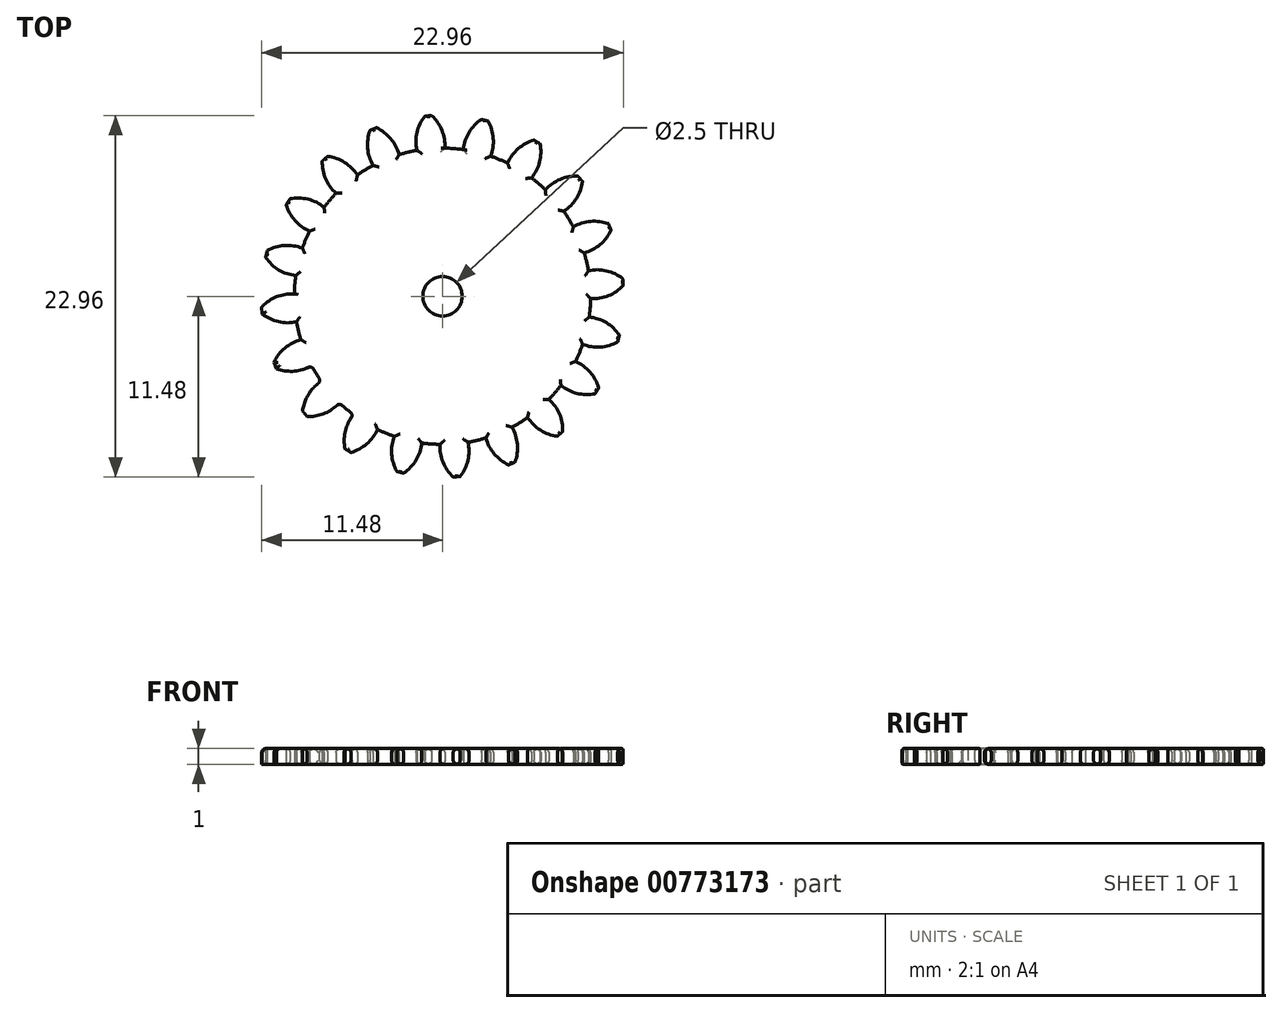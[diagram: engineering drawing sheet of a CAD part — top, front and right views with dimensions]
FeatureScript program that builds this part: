
annotation { "Feature Type Name" : "Feature", "Feature Type Description" : "" }
export const myFeature = defineFeature(function(context is Context, id is Id, definition is map)
    precondition{}
    {
        {
            assignVariable(context, id + "F0", {"name" : "GearDepth", "anyValue" : 1});
        }
        {
            assignVariable(context, id + "F1", {"name" : "TeethFillet", "anyValue" : getVariable(context, 'GearDepth') * .25});
        }
        {
            var Q0;
            Q0=qCreatedBy(makeId("Top.planeOp"),FACE);
            var sketch = newSketch(context, id + "F2", { "sketchPlane" : qUnion([Q0])});
            skCircle(sketch, "E0", {"center": v(0, 0) * mm, "radius": 9.4 * mm});
            skCircle(sketch, "E1", {"center": v(0, 0) * mm, "radius": 10.45 * mm, "construction": true});
            skCircle(sketch, "E2", {"center": v(0, 0) * mm, "radius": 11.5 * mm, "construction": true});
            skLineSegment(sketch, "E3", {"start": v(0, 0) * mm, "end": v(0, 17.6) * mm, "construction": true});
            skLineSegment(sketch, "E4", {"start": v(0, 0) * mm, "end": v(-1.42, 18) * mm, "construction": true});
            skLineSegment(sketch, "E5", {"start": v(0, 10.45) * mm, "end": v(-10.54, 10.45) * mm, "construction": true});
            skLineSegment(sketch, "E6", {"start": v(0, 10.45) * mm, "end": v(-10.3, 6.7) * mm, "construction": true});
            skCircle(sketch, "E7", {"center": v(0, 10.45) * mm, "radius": 2.61 * mm, "construction": true});
            skCircle(sketch, "E8", {"center": v(-2.46, 9.56) * mm, "radius": 2.61 * mm, "construction": true});
            skArc(sketch, "E9", {"start": v(-4.91, 10.45) * mm, "mid": v(-4.92, 10.42) * mm, "end": v(-4.94, 10.39) * mm});
            skArc(sketch, "E10.trimOffspring", {"start": v(0.15, 9.4) * mm, "mid": v(-0.03, 10.54) * mm, "end": v(-0.68, 11.48) * mm});
            skArc(sketch, "E11.MirrorCS", {"start": v(-1.62, 9.27) * mm, "mid": v(-1.62, 10.41) * mm, "end": v(-1.12, 11.45) * mm});
            skLineSegment(sketch, "E12", {"start": v(-1.12, 11.45) * mm, "end": v(-0.68, 11.48) * mm});
            skArc(sketch, "E13.1.0", {"start": v(-2.76, 9) * mm, "mid": v(-3.29, 10.01) * mm, "end": v(-4.2, 10.7) * mm});
            skLineSegment(sketch, "E13.1.1", {"start": v(-4.6, 10.54) * mm, "end": v(-4.2, 10.7) * mm});
            skArc(sketch, "E13.1.2", {"start": v(-4.4, 8.31) * mm, "mid": v(-4.76, 9.4) * mm, "end": v(-4.6, 10.54) * mm});
            skArc(sketch, "E13.2.0", {"start": v(-5.4, 7.7) * mm, "mid": v(-6.22, 8.5) * mm, "end": v(-7.3, 8.89) * mm});
            skLineSegment(sketch, "E13.2.1", {"start": v(-7.64, 8.6) * mm, "end": v(-7.3, 8.89) * mm});
            skArc(sketch, "E13.2.2", {"start": v(-6.76, 6.54) * mm, "mid": v(-7.43, 7.47) * mm, "end": v(-7.64, 8.6) * mm});
            skArc(sketch, "E13.3.0", {"start": v(-7.52, 5.65) * mm, "mid": v(-8.54, 6.17) * mm, "end": v(-9.69, 6.2) * mm});
            skLineSegment(sketch, "E13.3.1", {"start": v(-9.92, 5.82) * mm, "end": v(-9.69, 6.2) * mm});
            skArc(sketch, "E13.3.2", {"start": v(-8.45, 4.13) * mm, "mid": v(-9.37, 4.81) * mm, "end": v(-9.92, 5.82) * mm});
            skArc(sketch, "E13.4.0", {"start": v(-8.9, 3.05) * mm, "mid": v(-10.03, 3.23) * mm, "end": v(-11.13, 2.9) * mm});
            skLineSegment(sketch, "E13.4.1", {"start": v(-11.23, 2.47) * mm, "end": v(-11.13, 2.9) * mm});
            skArc(sketch, "E13.4.2", {"start": v(-9.32, 1.32) * mm, "mid": v(-10.4, 1.68) * mm, "end": v(-11.23, 2.47) * mm});
            skArc(sketch, "E13.5.0", {"start": v(-9.4, 0.15) * mm, "mid": v(-10.54, -0.03) * mm, "end": v(-11.48, -0.68) * mm});
            skLineSegment(sketch, "E13.5.1", {"start": v(-11.45, -1.12) * mm, "end": v(-11.48, -0.68) * mm});
            skArc(sketch, "E13.5.2", {"start": v(-9.27, -1.62) * mm, "mid": v(-10.41, -1.62) * mm, "end": v(-11.45, -1.12) * mm});
            skArc(sketch, "E13.6.0", {"start": v(-9, -2.76) * mm, "mid": v(-10.01, -3.29) * mm, "end": v(-10.7, -4.2) * mm});
            skLineSegment(sketch, "E13.6.1", {"start": v(-10.54, -4.6) * mm, "end": v(-10.7, -4.2) * mm});
            skArc(sketch, "E13.6.2", {"start": v(-8.31, -4.4) * mm, "mid": v(-9.4, -4.76) * mm, "end": v(-10.54, -4.6) * mm});
            skArc(sketch, "E13.7.0", {"start": v(-7.7, -5.4) * mm, "mid": v(-8.5, -6.22) * mm, "end": v(-8.89, -7.3) * mm});
            skLineSegment(sketch, "E13.7.1", {"start": v(-8.6, -7.64) * mm, "end": v(-8.89, -7.3) * mm});
            skArc(sketch, "E13.7.2", {"start": v(-6.54, -6.76) * mm, "mid": v(-7.47, -7.43) * mm, "end": v(-8.6, -7.64) * mm});
            skArc(sketch, "E13.8.0", {"start": v(-5.65, -7.52) * mm, "mid": v(-6.17, -8.54) * mm, "end": v(-6.2, -9.69) * mm});
            skLineSegment(sketch, "E13.8.1", {"start": v(-5.82, -9.92) * mm, "end": v(-6.2, -9.69) * mm});
            skArc(sketch, "E13.8.2", {"start": v(-4.13, -8.45) * mm, "mid": v(-4.81, -9.37) * mm, "end": v(-5.82, -9.92) * mm});
            skArc(sketch, "E13.9.0", {"start": v(-3.05, -8.9) * mm, "mid": v(-3.23, -10.03) * mm, "end": v(-2.9, -11.13) * mm});
            skLineSegment(sketch, "E13.9.1", {"start": v(-2.47, -11.23) * mm, "end": v(-2.9, -11.13) * mm});
            skArc(sketch, "E13.9.2", {"start": v(-1.32, -9.32) * mm, "mid": v(-1.68, -10.4) * mm, "end": v(-2.47, -11.23) * mm});
            skArc(sketch, "E13.10.0", {"start": v(-0.15, -9.4) * mm, "mid": v(0.03, -10.54) * mm, "end": v(0.68, -11.48) * mm});
            skLineSegment(sketch, "E13.10.1", {"start": v(1.12, -11.45) * mm, "end": v(0.68, -11.48) * mm});
            skArc(sketch, "E13.10.2", {"start": v(1.62, -9.27) * mm, "mid": v(1.62, -10.41) * mm, "end": v(1.12, -11.45) * mm});
            skArc(sketch, "E13.11.0", {"start": v(2.76, -9) * mm, "mid": v(3.29, -10.01) * mm, "end": v(4.2, -10.7) * mm});
            skLineSegment(sketch, "E13.11.1", {"start": v(4.6, -10.54) * mm, "end": v(4.2, -10.7) * mm});
            skArc(sketch, "E13.11.2", {"start": v(4.4, -8.31) * mm, "mid": v(4.76, -9.4) * mm, "end": v(4.6, -10.54) * mm});
            skArc(sketch, "E13.12.0", {"start": v(5.4, -7.7) * mm, "mid": v(6.22, -8.5) * mm, "end": v(7.3, -8.89) * mm});
            skLineSegment(sketch, "E13.12.1", {"start": v(7.64, -8.6) * mm, "end": v(7.3, -8.89) * mm});
            skArc(sketch, "E13.12.2", {"start": v(6.76, -6.54) * mm, "mid": v(7.43, -7.47) * mm, "end": v(7.64, -8.6) * mm});
            skArc(sketch, "E13.13.0", {"start": v(7.52, -5.65) * mm, "mid": v(8.54, -6.17) * mm, "end": v(9.69, -6.2) * mm});
            skLineSegment(sketch, "E13.13.1", {"start": v(9.92, -5.82) * mm, "end": v(9.69, -6.2) * mm});
            skArc(sketch, "E13.13.2", {"start": v(8.45, -4.13) * mm, "mid": v(9.37, -4.81) * mm, "end": v(9.92, -5.82) * mm});
            skArc(sketch, "E13.14.0", {"start": v(8.9, -3.05) * mm, "mid": v(10.03, -3.23) * mm, "end": v(11.13, -2.9) * mm});
            skLineSegment(sketch, "E13.14.1", {"start": v(11.23, -2.47) * mm, "end": v(11.13, -2.9) * mm});
            skArc(sketch, "E13.14.2", {"start": v(9.32, -1.32) * mm, "mid": v(10.4, -1.68) * mm, "end": v(11.23, -2.47) * mm});
            skArc(sketch, "E13.15.0", {"start": v(9.4, -0.15) * mm, "mid": v(10.54, 0.03) * mm, "end": v(11.48, 0.68) * mm});
            skLineSegment(sketch, "E13.15.1", {"start": v(11.45, 1.12) * mm, "end": v(11.48, 0.68) * mm});
            skArc(sketch, "E13.15.2", {"start": v(9.27, 1.62) * mm, "mid": v(10.41, 1.62) * mm, "end": v(11.45, 1.12) * mm});
            skArc(sketch, "E13.16.0", {"start": v(9, 2.76) * mm, "mid": v(10.01, 3.29) * mm, "end": v(10.7, 4.2) * mm});
            skLineSegment(sketch, "E13.16.1", {"start": v(10.54, 4.6) * mm, "end": v(10.7, 4.2) * mm});
            skArc(sketch, "E13.16.2", {"start": v(8.31, 4.4) * mm, "mid": v(9.4, 4.76) * mm, "end": v(10.54, 4.6) * mm});
            skArc(sketch, "E13.17.0", {"start": v(7.7, 5.4) * mm, "mid": v(8.5, 6.22) * mm, "end": v(8.89, 7.3) * mm});
            skLineSegment(sketch, "E13.17.1", {"start": v(8.6, 7.64) * mm, "end": v(8.89, 7.3) * mm});
            skArc(sketch, "E13.17.2", {"start": v(6.54, 6.76) * mm, "mid": v(7.47, 7.43) * mm, "end": v(8.6, 7.64) * mm});
            skArc(sketch, "E13.18.0", {"start": v(5.65, 7.52) * mm, "mid": v(6.17, 8.54) * mm, "end": v(6.2, 9.69) * mm});
            skLineSegment(sketch, "E13.18.1", {"start": v(5.82, 9.92) * mm, "end": v(6.2, 9.69) * mm});
            skArc(sketch, "E13.18.2", {"start": v(4.13, 8.45) * mm, "mid": v(4.81, 9.37) * mm, "end": v(5.82, 9.92) * mm});
            skArc(sketch, "E13.19.0", {"start": v(3.05, 8.9) * mm, "mid": v(3.23, 10.03) * mm, "end": v(2.9, 11.13) * mm});
            skLineSegment(sketch, "E13.19.1", {"start": v(2.47, 11.23) * mm, "end": v(2.9, 11.13) * mm});
            skArc(sketch, "E13.19.2", {"start": v(1.32, 9.32) * mm, "mid": v(1.68, 10.4) * mm, "end": v(2.47, 11.23) * mm});
            skCircle(sketch, "E14", {"center": v(0, 0) * mm, "radius": 1.25 * mm});
            skSolve(sketch);
        }
        {
            var Q0;
            {var subQ0=sQuery(id+"F2.wireOp",EDGE,"E10.trimOffspring");Q0=makeQuery(id+"F2.imprint","IMPRINT",FACE,{"disambiguationData":[TD([[makeQuery(id+"F2.imprint","IMPRINT",EDGE,{"derivedFrom":subQ0}),1.0]])]});}
            var Q1;
            {var subQ0=sQuery(id+"F2.wireOp",EDGE,"E0");var subQ1=makeQuery(id+"F2.imprint","INTERSECT",VERTEX,{"derivedFrom":[subQ0,sQuery(id+"F2.wireOp",EDGE,"E10.trimOffspring")]});Q1=makeQuery(id+"F2.imprint","IMPRINT",FACE,{"disambiguationData":[TD([[makeQuery(id+"F2.imprint","IMPRINT",EDGE,{"disambiguationData":[TD([[subQ1,-1.0]])],"derivedFrom":subQ0}),1.0]])]});}
            var Q2;
            {var subQ0=sQuery(id+"F2.wireOp",EDGE,"E13.1.0");Q2=makeQuery(id+"F2.imprint","IMPRINT",FACE,{"disambiguationData":[TD([[makeQuery(id+"F2.imprint","IMPRINT",EDGE,{"derivedFrom":subQ0}),1.0]])]});}
            var Q3;
            {var subQ0=sQuery(id+"F2.wireOp",EDGE,"E13.2.0");Q3=makeQuery(id+"F2.imprint","IMPRINT",FACE,{"disambiguationData":[TD([[makeQuery(id+"F2.imprint","IMPRINT",EDGE,{"derivedFrom":subQ0}),1.0]])]});}
            var Q4;
            {var subQ0=sQuery(id+"F2.wireOp",EDGE,"E13.3.0");Q4=makeQuery(id+"F2.imprint","IMPRINT",FACE,{"disambiguationData":[TD([[makeQuery(id+"F2.imprint","IMPRINT",EDGE,{"derivedFrom":subQ0}),1.0]])]});}
            var Q5;
            {var subQ0=sQuery(id+"F2.wireOp",EDGE,"E13.4.0");Q5=makeQuery(id+"F2.imprint","IMPRINT",FACE,{"disambiguationData":[TD([[makeQuery(id+"F2.imprint","IMPRINT",EDGE,{"derivedFrom":subQ0}),1.0]])]});}
            var Q6;
            {var subQ0=sQuery(id+"F2.wireOp",EDGE,"E13.5.0");Q6=makeQuery(id+"F2.imprint","IMPRINT",FACE,{"disambiguationData":[TD([[makeQuery(id+"F2.imprint","IMPRINT",EDGE,{"derivedFrom":subQ0}),1.0]])]});}
            var Q7;
            {var subQ0=sQuery(id+"F2.wireOp",EDGE,"E13.6.0");Q7=makeQuery(id+"F2.imprint","IMPRINT",FACE,{"disambiguationData":[TD([[makeQuery(id+"F2.imprint","IMPRINT",EDGE,{"derivedFrom":subQ0}),1.0]])]});}
            var Q8;
            {var subQ0=sQuery(id+"F2.wireOp",EDGE,"E13.7.0");Q8=makeQuery(id+"F2.imprint","IMPRINT",FACE,{"disambiguationData":[TD([[makeQuery(id+"F2.imprint","IMPRINT",EDGE,{"derivedFrom":subQ0}),1.0]])]});}
            var Q9;
            {var subQ0=sQuery(id+"F2.wireOp",EDGE,"E13.8.0");Q9=makeQuery(id+"F2.imprint","IMPRINT",FACE,{"disambiguationData":[TD([[makeQuery(id+"F2.imprint","IMPRINT",EDGE,{"derivedFrom":subQ0}),1.0]])]});}
            var Q10;
            {var subQ0=sQuery(id+"F2.wireOp",EDGE,"E13.9.0");Q10=makeQuery(id+"F2.imprint","IMPRINT",FACE,{"disambiguationData":[TD([[makeQuery(id+"F2.imprint","IMPRINT",EDGE,{"derivedFrom":subQ0}),1.0]])]});}
            var Q11;
            {var subQ0=sQuery(id+"F2.wireOp",EDGE,"E13.10.0");Q11=makeQuery(id+"F2.imprint","IMPRINT",FACE,{"disambiguationData":[TD([[makeQuery(id+"F2.imprint","IMPRINT",EDGE,{"derivedFrom":subQ0}),1.0]])]});}
            var Q12;
            {var subQ0=sQuery(id+"F2.wireOp",EDGE,"E13.11.0");Q12=makeQuery(id+"F2.imprint","IMPRINT",FACE,{"disambiguationData":[TD([[makeQuery(id+"F2.imprint","IMPRINT",EDGE,{"derivedFrom":subQ0}),1.0]])]});}
            var Q13;
            {var subQ0=sQuery(id+"F2.wireOp",EDGE,"E13.12.0");Q13=makeQuery(id+"F2.imprint","IMPRINT",FACE,{"disambiguationData":[TD([[makeQuery(id+"F2.imprint","IMPRINT",EDGE,{"derivedFrom":subQ0}),1.0]])]});}
            var Q14;
            {var subQ0=sQuery(id+"F2.wireOp",EDGE,"E13.13.0");Q14=makeQuery(id+"F2.imprint","IMPRINT",FACE,{"disambiguationData":[TD([[makeQuery(id+"F2.imprint","IMPRINT",EDGE,{"derivedFrom":subQ0}),1.0]])]});}
            var Q15;
            {var subQ0=sQuery(id+"F2.wireOp",EDGE,"E13.14.0");Q15=makeQuery(id+"F2.imprint","IMPRINT",FACE,{"disambiguationData":[TD([[makeQuery(id+"F2.imprint","IMPRINT",EDGE,{"derivedFrom":subQ0}),1.0]])]});}
            var Q16;
            {var subQ0=sQuery(id+"F2.wireOp",EDGE,"E13.15.0");Q16=makeQuery(id+"F2.imprint","IMPRINT",FACE,{"disambiguationData":[TD([[makeQuery(id+"F2.imprint","IMPRINT",EDGE,{"derivedFrom":subQ0}),1.0]])]});}
            var Q17;
            {var subQ0=sQuery(id+"F2.wireOp",EDGE,"E13.16.0");Q17=makeQuery(id+"F2.imprint","IMPRINT",FACE,{"disambiguationData":[TD([[makeQuery(id+"F2.imprint","IMPRINT",EDGE,{"derivedFrom":subQ0}),1.0]])]});}
            var Q18;
            {var subQ0=sQuery(id+"F2.wireOp",EDGE,"E13.17.0");Q18=makeQuery(id+"F2.imprint","IMPRINT",FACE,{"disambiguationData":[TD([[makeQuery(id+"F2.imprint","IMPRINT",EDGE,{"derivedFrom":subQ0}),1.0]])]});}
            var Q19;
            {var subQ0=sQuery(id+"F2.wireOp",EDGE,"E13.18.0");Q19=makeQuery(id+"F2.imprint","IMPRINT",FACE,{"disambiguationData":[TD([[makeQuery(id+"F2.imprint","IMPRINT",EDGE,{"derivedFrom":subQ0}),1.0]])]});}
            var Q20;
            {var subQ0=sQuery(id+"F2.wireOp",EDGE,"E13.19.0");Q20=makeQuery(id+"F2.imprint","IMPRINT",FACE,{"disambiguationData":[TD([[makeQuery(id+"F2.imprint","IMPRINT",EDGE,{"derivedFrom":subQ0}),1.0]])]});}
            var Q21;
            Q21=sQuery(id+"F2.wireOp",EDGE,"E0");
            var Q22;
            Q22=sQuery(id+"F2.wireOp",EDGE,"E10.trimOffspring");
            var Q23;
            Q23=sQuery(id+"F2.wireOp",EDGE,"E12");
            var Q24;
            Q24=sQuery(id+"F2.wireOp",EDGE,"E11.MirrorCS");
            extrude(context, id + "F3", {"entities" : qUnion([Q0, Q1, Q2, Q3, Q4, Q5, Q6, Q7, Q8, Q9, Q10, Q11, Q12, Q13, Q14, Q15, Q16, Q17, Q18, Q19, Q20]), "surfaceEntities" : qUnion([Q21, Q22, Q23, Q24]), "depth" : (getVariable(context, 'GearDepth')) * mm});
        }
        {
            var Q0;
            Q0=makeQuery(id+"F3.opExtrude","CAP_EDGE",EDGE,{"disambiguationData":[OSD([sQuery(id+"F2.wireOp",EDGE,"E13.5.2")])],"isStart":false});
            var Q1;
            Q1=makeQuery(id+"F3.opExtrude","CAP_EDGE",EDGE,{"disambiguationData":[OSD([sQuery(id+"F2.wireOp",EDGE,"E13.5.1")])],"isStart":false});
            var Q2;
            {var subQ0=sQuery(id+"F2.wireOp",EDGE,"E0");Q2=makeQuery(id+"F3.opExtrude","CAP_EDGE",EDGE,{"disambiguationData":[OSD([subQ0]),TDD([makeQuery(id+"F2.imprint","IMPRINT",EDGE,{"disambiguationData":[TD([[makeQuery(id+"F2.imprint","INTERSECT",VERTEX,{"derivedFrom":[subQ0,sQuery(id+"F2.wireOp",EDGE,"E13.5.2")]}),-1.0]])],"derivedFrom":subQ0})])],"isStart":false});}
            var Q3;
            Q3=makeQuery(id+"F3.opExtrude","CAP_EDGE",EDGE,{"disambiguationData":[OSD([sQuery(id+"F2.wireOp",EDGE,"E13.6.0")])],"isStart":false});
            var Q4;
            Q4=makeQuery(id+"F3.opExtrude","CAP_EDGE",EDGE,{"disambiguationData":[OSD([sQuery(id+"F2.wireOp",EDGE,"E13.6.1")])],"isStart":false});
            var Q5;
            Q5=makeQuery(id+"F3.opExtrude","CAP_EDGE",EDGE,{"disambiguationData":[OSD([sQuery(id+"F2.wireOp",EDGE,"E13.6.2")])],"isStart":false});
            var Q6;
            {var subQ0=sQuery(id+"F2.wireOp",EDGE,"E0");Q6=makeQuery(id+"F3.opExtrude","SWEPT_FACE",FACE,{"disambiguationData":[OSD([subQ0]),TDD([makeQuery(id+"F2.imprint","IMPRINT",EDGE,{"disambiguationData":[TD([[makeQuery(id+"F2.imprint","INTERSECT",VERTEX,{"derivedFrom":[subQ0,sQuery(id+"F2.wireOp",EDGE,"E13.6.2")]}),-1.0]])],"derivedFrom":subQ0})])]});}
            var Q7;
            {var subQ0=sQuery(id+"F2.wireOp",EDGE,"E0");Q7=makeQuery(id+"F3.opExtrude","CAP_EDGE",EDGE,{"disambiguationData":[OSD([subQ0]),TDD([makeQuery(id+"F2.imprint","IMPRINT",EDGE,{"disambiguationData":[TD([[makeQuery(id+"F2.imprint","INTERSECT",VERTEX,{"derivedFrom":[subQ0,sQuery(id+"F2.wireOp",EDGE,"E13.6.2")]}),-1.0]])],"derivedFrom":subQ0})])],"isStart":false});}
            var Q8;
            Q8=makeQuery(id+"F3.opExtrude","CAP_EDGE",EDGE,{"disambiguationData":[OSD([sQuery(id+"F2.wireOp",EDGE,"E13.7.2")])],"isStart":true});
            var Q9;
            {var subQ0=sQuery(id+"F2.wireOp",EDGE,"E0");Q9=makeQuery(id+"F3.opExtrude","CAP_EDGE",EDGE,{"disambiguationData":[OSD([subQ0]),TDD([makeQuery(id+"F2.imprint","IMPRINT",EDGE,{"disambiguationData":[TD([[makeQuery(id+"F2.imprint","INTERSECT",VERTEX,{"derivedFrom":[subQ0,sQuery(id+"F2.wireOp",EDGE,"E13.7.2")]}),-1.0]])],"derivedFrom":subQ0})])],"isStart":true});}
            var Q10;
            Q10=makeQuery(id+"F3.opExtrude","CAP_EDGE",EDGE,{"disambiguationData":[OSD([sQuery(id+"F2.wireOp",EDGE,"E13.7.2")])],"isStart":false});
            var Q11;
            {var subQ0=sQuery(id+"F2.wireOp",EDGE,"E0");Q11=makeQuery(id+"F3.opExtrude","CAP_EDGE",EDGE,{"disambiguationData":[OSD([subQ0]),TDD([makeQuery(id+"F2.imprint","IMPRINT",EDGE,{"disambiguationData":[TD([[makeQuery(id+"F2.imprint","INTERSECT",VERTEX,{"derivedFrom":[subQ0,sQuery(id+"F2.wireOp",EDGE,"E13.7.2")]}),-1.0]])],"derivedFrom":subQ0})])],"isStart":false});}
            var Q12;
            Q12=makeQuery(id+"F3.opExtrude","CAP_EDGE",EDGE,{"disambiguationData":[OSD([sQuery(id+"F2.wireOp",EDGE,"E13.8.0")])],"isStart":false});
            var Q13;
            {var subQ0=sQuery(id+"F2.wireOp",EDGE,"E0");Q13=makeQuery(id+"F3.opExtrude","SWEPT_FACE",FACE,{"disambiguationData":[OSD([subQ0]),TDD([makeQuery(id+"F2.imprint","IMPRINT",EDGE,{"disambiguationData":[TD([[makeQuery(id+"F2.imprint","INTERSECT",VERTEX,{"derivedFrom":[subQ0,sQuery(id+"F2.wireOp",EDGE,"E13.7.2")]}),-1.0]])],"derivedFrom":subQ0})])]});}
            var Q14;
            Q14=makeQuery(id+"F3.opExtrude","CAP_EDGE",EDGE,{"disambiguationData":[OSD([sQuery(id+"F2.wireOp",EDGE,"E13.6.0")])],"isStart":true});
            var Q15;
            Q15=makeQuery(id+"F3.opExtrude","CAP_EDGE",EDGE,{"disambiguationData":[OSD([sQuery(id+"F2.wireOp",EDGE,"E13.8.2")])],"isStart":false});
            var Q16;
            {var subQ0=sQuery(id+"F2.wireOp",EDGE,"E0");Q16=makeQuery(id+"F3.opExtrude","CAP_EDGE",EDGE,{"disambiguationData":[OSD([subQ0]),TDD([makeQuery(id+"F2.imprint","IMPRINT",EDGE,{"disambiguationData":[TD([[makeQuery(id+"F2.imprint","INTERSECT",VERTEX,{"derivedFrom":[subQ0,sQuery(id+"F2.wireOp",EDGE,"E13.8.2")]}),-1.0]])],"derivedFrom":subQ0})])],"isStart":false});}
            var Q17;
            Q17=makeQuery(id+"F3.opExtrude","CAP_EDGE",EDGE,{"disambiguationData":[OSD([sQuery(id+"F2.wireOp",EDGE,"E13.9.0")])],"isStart":false});
            var Q18;
            Q18=makeQuery(id+"F3.opExtrude","CAP_EDGE",EDGE,{"disambiguationData":[OSD([sQuery(id+"F2.wireOp",EDGE,"E13.9.2")])],"isStart":false});
            var Q19;
            {var subQ0=sQuery(id+"F2.wireOp",EDGE,"E0");Q19=makeQuery(id+"F3.opExtrude","CAP_EDGE",EDGE,{"disambiguationData":[OSD([subQ0]),TDD([makeQuery(id+"F2.imprint","IMPRINT",EDGE,{"disambiguationData":[TD([[makeQuery(id+"F2.imprint","INTERSECT",VERTEX,{"derivedFrom":[subQ0,sQuery(id+"F2.wireOp",EDGE,"E13.9.2")]}),-1.0]])],"derivedFrom":subQ0})])],"isStart":false});}
            var Q20;
            Q20=makeQuery(id+"F3.opExtrude","CAP_EDGE",EDGE,{"disambiguationData":[OSD([sQuery(id+"F2.wireOp",EDGE,"E13.10.0")])],"isStart":false});
            var Q21;
            Q21=makeQuery(id+"F3.opExtrude","CAP_EDGE",EDGE,{"disambiguationData":[OSD([sQuery(id+"F2.wireOp",EDGE,"E13.10.2")])],"isStart":false});
            var Q22;
            {var subQ0=sQuery(id+"F2.wireOp",EDGE,"E0");Q22=makeQuery(id+"F3.opExtrude","CAP_EDGE",EDGE,{"disambiguationData":[OSD([subQ0]),TDD([makeQuery(id+"F2.imprint","IMPRINT",EDGE,{"disambiguationData":[TD([[makeQuery(id+"F2.imprint","INTERSECT",VERTEX,{"derivedFrom":[subQ0,sQuery(id+"F2.wireOp",EDGE,"E13.10.2")]}),-1.0]])],"derivedFrom":subQ0})])],"isStart":false});}
            var Q23;
            Q23=makeQuery(id+"F3.opExtrude","CAP_EDGE",EDGE,{"disambiguationData":[OSD([sQuery(id+"F2.wireOp",EDGE,"E13.11.0")])],"isStart":false});
            var Q24;
            Q24=makeQuery(id+"F3.opExtrude","CAP_EDGE",EDGE,{"disambiguationData":[OSD([sQuery(id+"F2.wireOp",EDGE,"E13.11.2")])],"isStart":false});
            var Q25;
            {var subQ0=sQuery(id+"F2.wireOp",EDGE,"E0");Q25=makeQuery(id+"F3.opExtrude","CAP_EDGE",EDGE,{"disambiguationData":[OSD([subQ0]),TDD([makeQuery(id+"F2.imprint","IMPRINT",EDGE,{"disambiguationData":[TD([[makeQuery(id+"F2.imprint","INTERSECT",VERTEX,{"derivedFrom":[subQ0,sQuery(id+"F2.wireOp",EDGE,"E13.11.2")]}),-1.0]])],"derivedFrom":subQ0})])],"isStart":false});}
            var Q26;
            Q26=makeQuery(id+"F3.opExtrude","CAP_EDGE",EDGE,{"disambiguationData":[OSD([sQuery(id+"F2.wireOp",EDGE,"E13.12.0")])],"isStart":false});
            var Q27;
            Q27=makeQuery(id+"F3.opExtrude","CAP_EDGE",EDGE,{"disambiguationData":[OSD([sQuery(id+"F2.wireOp",EDGE,"E13.12.2")])],"isStart":false});
            var Q28;
            {var subQ0=sQuery(id+"F2.wireOp",EDGE,"E0");Q28=makeQuery(id+"F3.opExtrude","CAP_EDGE",EDGE,{"disambiguationData":[OSD([subQ0]),TDD([makeQuery(id+"F2.imprint","IMPRINT",EDGE,{"disambiguationData":[TD([[makeQuery(id+"F2.imprint","INTERSECT",VERTEX,{"derivedFrom":[subQ0,sQuery(id+"F2.wireOp",EDGE,"E13.12.2")]}),-1.0]])],"derivedFrom":subQ0})])],"isStart":false});}
            var Q29;
            Q29=makeQuery(id+"F3.opExtrude","CAP_EDGE",EDGE,{"disambiguationData":[OSD([sQuery(id+"F2.wireOp",EDGE,"E13.13.0")])],"isStart":false});
            var Q30;
            Q30=makeQuery(id+"F3.opExtrude","CAP_EDGE",EDGE,{"disambiguationData":[OSD([sQuery(id+"F2.wireOp",EDGE,"E13.13.2")])],"isStart":false});
            var Q31;
            {var subQ0=sQuery(id+"F2.wireOp",EDGE,"E0");Q31=makeQuery(id+"F3.opExtrude","CAP_EDGE",EDGE,{"disambiguationData":[OSD([subQ0]),TDD([makeQuery(id+"F2.imprint","IMPRINT",EDGE,{"disambiguationData":[TD([[makeQuery(id+"F2.imprint","INTERSECT",VERTEX,{"derivedFrom":[subQ0,sQuery(id+"F2.wireOp",EDGE,"E13.13.2")]}),-1.0]])],"derivedFrom":subQ0})])],"isStart":false});}
            var Q32;
            Q32=makeQuery(id+"F3.opExtrude","CAP_EDGE",EDGE,{"disambiguationData":[OSD([sQuery(id+"F2.wireOp",EDGE,"E13.14.0")])],"isStart":false});
            var Q33;
            Q33=makeQuery(id+"F3.opExtrude","CAP_EDGE",EDGE,{"disambiguationData":[OSD([sQuery(id+"F2.wireOp",EDGE,"E13.14.2")])],"isStart":false});
            var Q34;
            {var subQ0=sQuery(id+"F2.wireOp",EDGE,"E0");Q34=makeQuery(id+"F3.opExtrude","CAP_EDGE",EDGE,{"disambiguationData":[OSD([subQ0]),TDD([makeQuery(id+"F2.imprint","IMPRINT",EDGE,{"disambiguationData":[TD([[makeQuery(id+"F2.imprint","INTERSECT",VERTEX,{"derivedFrom":[subQ0,sQuery(id+"F2.wireOp",EDGE,"E13.14.2")]}),-1.0]])],"derivedFrom":subQ0})])],"isStart":false});}
            var Q35;
            Q35=makeQuery(id+"F3.opExtrude","CAP_EDGE",EDGE,{"disambiguationData":[OSD([sQuery(id+"F2.wireOp",EDGE,"E13.15.0")])],"isStart":false});
            var Q36;
            {var subQ0=sQuery(id+"F2.wireOp",EDGE,"E0");Q36=makeQuery(id+"F3.opExtrude","CAP_EDGE",EDGE,{"disambiguationData":[OSD([subQ0]),TDD([makeQuery(id+"F2.imprint","IMPRINT",EDGE,{"disambiguationData":[TD([[makeQuery(id+"F2.imprint","INTERSECT",VERTEX,{"derivedFrom":[subQ0,sQuery(id+"F2.wireOp",EDGE,"E13.14.2")]}),-1.0]])],"derivedFrom":subQ0})])],"isStart":false});}
            var Q37;
            Q37=makeQuery(id+"F3.opExtrude","CAP_EDGE",EDGE,{"disambiguationData":[OSD([sQuery(id+"F2.wireOp",EDGE,"E13.15.2")])],"isStart":false});
            var Q38;
            {var subQ0=sQuery(id+"F2.wireOp",EDGE,"E0");Q38=makeQuery(id+"F3.opExtrude","CAP_EDGE",EDGE,{"disambiguationData":[OSD([subQ0]),TDD([makeQuery(id+"F2.imprint","IMPRINT",EDGE,{"disambiguationData":[TD([[makeQuery(id+"F2.imprint","INTERSECT",VERTEX,{"derivedFrom":[subQ0,sQuery(id+"F2.wireOp",EDGE,"E13.15.2")]}),-1.0]])],"derivedFrom":subQ0})])],"isStart":false});}
            var Q39;
            Q39=makeQuery(id+"F3.opExtrude","CAP_EDGE",EDGE,{"disambiguationData":[OSD([sQuery(id+"F2.wireOp",EDGE,"E13.16.0")])],"isStart":false});
            var Q40;
            Q40=makeQuery(id+"F3.opExtrude","CAP_EDGE",EDGE,{"disambiguationData":[OSD([sQuery(id+"F2.wireOp",EDGE,"E13.16.2")])],"isStart":false});
            var Q41;
            Q41=makeQuery(id+"F3.opExtrude","CAP_EDGE",EDGE,{"disambiguationData":[OSD([sQuery(id+"F2.wireOp",EDGE,"E13.17.0")])],"isStart":false});
            var Q42;
            {var subQ0=sQuery(id+"F2.wireOp",EDGE,"E0");Q42=makeQuery(id+"F3.opExtrude","CAP_EDGE",EDGE,{"disambiguationData":[OSD([subQ0]),TDD([makeQuery(id+"F2.imprint","IMPRINT",EDGE,{"disambiguationData":[TD([[makeQuery(id+"F2.imprint","INTERSECT",VERTEX,{"derivedFrom":[subQ0,sQuery(id+"F2.wireOp",EDGE,"E13.16.2")]}),-1.0]])],"derivedFrom":subQ0})])],"isStart":false});}
            var Q43;
            Q43=makeQuery(id+"F3.opExtrude","CAP_EDGE",EDGE,{"disambiguationData":[OSD([sQuery(id+"F2.wireOp",EDGE,"E13.17.2")])],"isStart":false});
            var Q44;
            {var subQ0=sQuery(id+"F2.wireOp",EDGE,"E0");Q44=makeQuery(id+"F3.opExtrude","CAP_EDGE",EDGE,{"disambiguationData":[OSD([subQ0]),TDD([makeQuery(id+"F2.imprint","IMPRINT",EDGE,{"disambiguationData":[TD([[makeQuery(id+"F2.imprint","INTERSECT",VERTEX,{"derivedFrom":[subQ0,sQuery(id+"F2.wireOp",EDGE,"E13.17.2")]}),-1.0]])],"derivedFrom":subQ0})])],"isStart":false});}
            var Q45;
            Q45=makeQuery(id+"F3.opExtrude","CAP_EDGE",EDGE,{"disambiguationData":[OSD([sQuery(id+"F2.wireOp",EDGE,"E13.18.0")])],"isStart":false});
            var Q46;
            Q46=makeQuery(id+"F3.opExtrude","CAP_EDGE",EDGE,{"disambiguationData":[OSD([sQuery(id+"F2.wireOp",EDGE,"E13.18.2")])],"isStart":false});
            var Q47;
            {var subQ0=sQuery(id+"F2.wireOp",EDGE,"E0");Q47=makeQuery(id+"F3.opExtrude","CAP_EDGE",EDGE,{"disambiguationData":[OSD([subQ0]),TDD([makeQuery(id+"F2.imprint","IMPRINT",EDGE,{"disambiguationData":[TD([[makeQuery(id+"F2.imprint","INTERSECT",VERTEX,{"derivedFrom":[subQ0,sQuery(id+"F2.wireOp",EDGE,"E13.18.2")]}),-1.0]])],"derivedFrom":subQ0})])],"isStart":false});}
            var Q48;
            Q48=makeQuery(id+"F3.opExtrude","CAP_EDGE",EDGE,{"disambiguationData":[OSD([sQuery(id+"F2.wireOp",EDGE,"E13.19.0")])],"isStart":false});
            var Q49;
            Q49=makeQuery(id+"F3.opExtrude","CAP_EDGE",EDGE,{"disambiguationData":[OSD([sQuery(id+"F2.wireOp",EDGE,"E13.19.2")])],"isStart":false});
            var Q50;
            Q50=makeQuery(id+"F3.opExtrude","CAP_EDGE",EDGE,{"disambiguationData":[OSD([sQuery(id+"F2.wireOp",EDGE,"E10.trimOffspring")])],"isStart":false});
            var Q51;
            Q51=makeQuery(id+"F3.opExtrude","CAP_EDGE",EDGE,{"disambiguationData":[OSD([sQuery(id+"F2.wireOp",EDGE,"E11.MirrorCS")])],"isStart":false});
            var Q52;
            {var subQ0=sQuery(id+"F2.wireOp",EDGE,"E0");Q52=makeQuery(id+"F3.opExtrude","CAP_EDGE",EDGE,{"disambiguationData":[OSD([subQ0]),TDD([makeQuery(id+"F2.imprint","IMPRINT",EDGE,{"disambiguationData":[TD([[makeQuery(id+"F2.imprint","INTERSECT",VERTEX,{"derivedFrom":[subQ0,sQuery(id+"F2.wireOp",EDGE,"E11.MirrorCS")]}),-1.0]])],"derivedFrom":subQ0})])],"isStart":false});}
            var Q53;
            Q53=makeQuery(id+"F3.opExtrude","CAP_EDGE",EDGE,{"disambiguationData":[OSD([sQuery(id+"F2.wireOp",EDGE,"E13.1.0")])],"isStart":false});
            var Q54;
            Q54=makeQuery(id+"F3.opExtrude","CAP_EDGE",EDGE,{"disambiguationData":[OSD([sQuery(id+"F2.wireOp",EDGE,"E13.1.2")])],"isStart":false});
            var Q55;
            {var subQ0=sQuery(id+"F2.wireOp",EDGE,"E0");Q55=makeQuery(id+"F3.opExtrude","CAP_EDGE",EDGE,{"disambiguationData":[OSD([subQ0]),TDD([makeQuery(id+"F2.imprint","IMPRINT",EDGE,{"disambiguationData":[TD([[makeQuery(id+"F2.imprint","INTERSECT",VERTEX,{"derivedFrom":[subQ0,sQuery(id+"F2.wireOp",EDGE,"E13.1.2")]}),-1.0]])],"derivedFrom":subQ0})])],"isStart":false});}
            var Q56;
            Q56=makeQuery(id+"F3.opExtrude","CAP_EDGE",EDGE,{"disambiguationData":[OSD([sQuery(id+"F2.wireOp",EDGE,"E13.2.0")])],"isStart":false});
            var Q57;
            Q57=makeQuery(id+"F3.opExtrude","CAP_EDGE",EDGE,{"disambiguationData":[OSD([sQuery(id+"F2.wireOp",EDGE,"E13.2.2")])],"isStart":false});
            var Q58;
            {var subQ0=sQuery(id+"F2.wireOp",EDGE,"E0");Q58=makeQuery(id+"F3.opExtrude","CAP_EDGE",EDGE,{"disambiguationData":[OSD([subQ0]),TDD([makeQuery(id+"F2.imprint","IMPRINT",EDGE,{"disambiguationData":[TD([[makeQuery(id+"F2.imprint","INTERSECT",VERTEX,{"derivedFrom":[subQ0,sQuery(id+"F2.wireOp",EDGE,"E13.2.2")]}),-1.0]])],"derivedFrom":subQ0})])],"isStart":false});}
            var Q59;
            Q59=makeQuery(id+"F3.opExtrude","CAP_EDGE",EDGE,{"disambiguationData":[OSD([sQuery(id+"F2.wireOp",EDGE,"E13.3.0")])],"isStart":false});
            var Q60;
            Q60=makeQuery(id+"F3.opExtrude","CAP_EDGE",EDGE,{"disambiguationData":[OSD([sQuery(id+"F2.wireOp",EDGE,"E13.3.2")])],"isStart":false});
            var Q61;
            {var subQ0=sQuery(id+"F2.wireOp",EDGE,"E0");Q61=makeQuery(id+"F3.opExtrude","CAP_EDGE",EDGE,{"disambiguationData":[OSD([subQ0]),TDD([makeQuery(id+"F2.imprint","IMPRINT",EDGE,{"disambiguationData":[TD([[makeQuery(id+"F2.imprint","INTERSECT",VERTEX,{"derivedFrom":[subQ0,sQuery(id+"F2.wireOp",EDGE,"E13.3.2")]}),-1.0]])],"derivedFrom":subQ0})])],"isStart":false});}
            var Q62;
            Q62=makeQuery(id+"F3.opExtrude","CAP_EDGE",EDGE,{"disambiguationData":[OSD([sQuery(id+"F2.wireOp",EDGE,"E13.4.0")])],"isStart":false});
            var Q63;
            Q63=makeQuery(id+"F3.opExtrude","CAP_EDGE",EDGE,{"disambiguationData":[OSD([sQuery(id+"F2.wireOp",EDGE,"E13.4.2")])],"isStart":false});
            var Q64;
            {var subQ0=sQuery(id+"F2.wireOp",EDGE,"E0");Q64=makeQuery(id+"F3.opExtrude","CAP_EDGE",EDGE,{"disambiguationData":[OSD([subQ0]),TDD([makeQuery(id+"F2.imprint","IMPRINT",EDGE,{"disambiguationData":[TD([[makeQuery(id+"F2.imprint","INTERSECT",VERTEX,{"derivedFrom":[subQ0,sQuery(id+"F2.wireOp",EDGE,"E13.4.2")]}),-1.0]])],"derivedFrom":subQ0})])],"isStart":false});}
            var Q65;
            {var subQ0=sQuery(id+"F2.wireOp",EDGE,"E0");Q65=makeQuery(id+"F3.opExtrude","CAP_EDGE",EDGE,{"disambiguationData":[OSD([subQ0]),TDD([makeQuery(id+"F2.imprint","IMPRINT",EDGE,{"disambiguationData":[TD([[makeQuery(id+"F2.imprint","INTERSECT",VERTEX,{"derivedFrom":[subQ0,sQuery(id+"F2.wireOp",EDGE,"E13.5.2")]}),-1.0]])],"derivedFrom":subQ0})])],"isStart":true});}
            var Q66;
            Q66=makeQuery(id+"F3.opExtrude","CAP_EDGE",EDGE,{"disambiguationData":[OSD([sQuery(id+"F2.wireOp",EDGE,"E13.5.2")])],"isStart":true});
            var Q67;
            {var subQ0=sQuery(id+"F2.wireOp",EDGE,"E0");Q67=makeQuery(id+"F3.opExtrude","CAP_EDGE",EDGE,{"disambiguationData":[OSD([subQ0]),TDD([makeQuery(id+"F2.imprint","IMPRINT",EDGE,{"disambiguationData":[TD([[makeQuery(id+"F2.imprint","INTERSECT",VERTEX,{"derivedFrom":[subQ0,sQuery(id+"F2.wireOp",EDGE,"E13.4.2")]}),-1.0]])],"derivedFrom":subQ0})])],"isStart":true});}
            var Q68;
            Q68=makeQuery(id+"F3.opExtrude","CAP_EDGE",EDGE,{"disambiguationData":[OSD([sQuery(id+"F2.wireOp",EDGE,"E13.4.2")])],"isStart":true});
            var Q69;
            Q69=makeQuery(id+"F3.opExtrude","CAP_EDGE",EDGE,{"disambiguationData":[OSD([sQuery(id+"F2.wireOp",EDGE,"E13.4.0")])],"isStart":true});
            var Q70;
            {var subQ0=sQuery(id+"F2.wireOp",EDGE,"E0");Q70=makeQuery(id+"F3.opExtrude","CAP_EDGE",EDGE,{"disambiguationData":[OSD([subQ0]),TDD([makeQuery(id+"F2.imprint","IMPRINT",EDGE,{"disambiguationData":[TD([[makeQuery(id+"F2.imprint","INTERSECT",VERTEX,{"derivedFrom":[subQ0,sQuery(id+"F2.wireOp",EDGE,"E13.3.2")]}),-1.0]])],"derivedFrom":subQ0})])],"isStart":true});}
            var Q71;
            Q71=makeQuery(id+"F3.opExtrude","CAP_EDGE",EDGE,{"disambiguationData":[OSD([sQuery(id+"F2.wireOp",EDGE,"E13.3.2")])],"isStart":true});
            var Q72;
            Q72=makeQuery(id+"F3.opExtrude","CAP_EDGE",EDGE,{"disambiguationData":[OSD([sQuery(id+"F2.wireOp",EDGE,"E13.3.0")])],"isStart":true});
            var Q73;
            {var subQ0=sQuery(id+"F2.wireOp",EDGE,"E0");Q73=makeQuery(id+"F3.opExtrude","CAP_EDGE",EDGE,{"disambiguationData":[OSD([subQ0]),TDD([makeQuery(id+"F2.imprint","IMPRINT",EDGE,{"disambiguationData":[TD([[makeQuery(id+"F2.imprint","INTERSECT",VERTEX,{"derivedFrom":[subQ0,sQuery(id+"F2.wireOp",EDGE,"E13.2.2")]}),-1.0]])],"derivedFrom":subQ0})])],"isStart":true});}
            var Q74;
            Q74=makeQuery(id+"F3.opExtrude","CAP_EDGE",EDGE,{"disambiguationData":[OSD([sQuery(id+"F2.wireOp",EDGE,"E13.2.2")])],"isStart":true});
            var Q75;
            Q75=makeQuery(id+"F3.opExtrude","CAP_EDGE",EDGE,{"disambiguationData":[OSD([sQuery(id+"F2.wireOp",EDGE,"E13.2.0")])],"isStart":true});
            var Q76;
            Q76=makeQuery(id+"F3.opExtrude","CAP_EDGE",EDGE,{"disambiguationData":[OSD([sQuery(id+"F2.wireOp",EDGE,"E13.1.2")])],"isStart":true});
            var Q77;
            {var subQ0=sQuery(id+"F2.wireOp",EDGE,"E0");Q77=makeQuery(id+"F3.opExtrude","CAP_EDGE",EDGE,{"disambiguationData":[OSD([subQ0]),TDD([makeQuery(id+"F2.imprint","IMPRINT",EDGE,{"disambiguationData":[TD([[makeQuery(id+"F2.imprint","INTERSECT",VERTEX,{"derivedFrom":[subQ0,sQuery(id+"F2.wireOp",EDGE,"E13.1.2")]}),-1.0]])],"derivedFrom":subQ0})])],"isStart":true});}
            var Q78;
            Q78=makeQuery(id+"F3.opExtrude","CAP_EDGE",EDGE,{"disambiguationData":[OSD([sQuery(id+"F2.wireOp",EDGE,"E13.1.0")])],"isStart":true});
            var Q79;
            {var subQ0=sQuery(id+"F2.wireOp",EDGE,"E0");Q79=makeQuery(id+"F3.opExtrude","CAP_EDGE",EDGE,{"disambiguationData":[OSD([subQ0]),TDD([makeQuery(id+"F2.imprint","IMPRINT",EDGE,{"disambiguationData":[TD([[makeQuery(id+"F2.imprint","INTERSECT",VERTEX,{"derivedFrom":[subQ0,sQuery(id+"F2.wireOp",EDGE,"E11.MirrorCS")]}),-1.0]])],"derivedFrom":subQ0})])],"isStart":true});}
            var Q80;
            Q80=makeQuery(id+"F3.opExtrude","CAP_EDGE",EDGE,{"disambiguationData":[OSD([sQuery(id+"F2.wireOp",EDGE,"E11.MirrorCS")])],"isStart":true});
            var Q81;
            Q81=makeQuery(id+"F3.opExtrude","CAP_EDGE",EDGE,{"disambiguationData":[OSD([sQuery(id+"F2.wireOp",EDGE,"E10.trimOffspring")])],"isStart":true});
            var Q82;
            {var subQ0=sQuery(id+"F2.wireOp",EDGE,"E0");Q82=makeQuery(id+"F3.opExtrude","CAP_EDGE",EDGE,{"disambiguationData":[OSD([subQ0]),TDD([makeQuery(id+"F2.imprint","IMPRINT",EDGE,{"disambiguationData":[TD([[makeQuery(id+"F2.imprint","INTERSECT",VERTEX,{"derivedFrom":[subQ0,sQuery(id+"F2.wireOp",EDGE,"E10.trimOffspring")]}),1.0]])],"derivedFrom":subQ0})])],"isStart":true});}
            var Q83;
            Q83=makeQuery(id+"F3.opExtrude","CAP_EDGE",EDGE,{"disambiguationData":[OSD([sQuery(id+"F2.wireOp",EDGE,"E13.19.2")])],"isStart":true});
            var Q84;
            Q84=makeQuery(id+"F3.opExtrude","CAP_EDGE",EDGE,{"disambiguationData":[OSD([sQuery(id+"F2.wireOp",EDGE,"E13.19.0")])],"isStart":true});
            var Q85;
            {var subQ0=sQuery(id+"F2.wireOp",EDGE,"E0");Q85=makeQuery(id+"F3.opExtrude","CAP_EDGE",EDGE,{"disambiguationData":[OSD([subQ0]),TDD([makeQuery(id+"F2.imprint","IMPRINT",EDGE,{"disambiguationData":[TD([[makeQuery(id+"F2.imprint","INTERSECT",VERTEX,{"derivedFrom":[subQ0,sQuery(id+"F2.wireOp",EDGE,"E13.18.2")]}),-1.0]])],"derivedFrom":subQ0})])],"isStart":true});}
            var Q86;
            Q86=makeQuery(id+"F3.opExtrude","CAP_EDGE",EDGE,{"disambiguationData":[OSD([sQuery(id+"F2.wireOp",EDGE,"E13.18.2")])],"isStart":true});
            var Q87;
            Q87=makeQuery(id+"F3.opExtrude","CAP_EDGE",EDGE,{"disambiguationData":[OSD([sQuery(id+"F2.wireOp",EDGE,"E13.18.0")])],"isStart":true});
            var Q88;
            {var subQ0=sQuery(id+"F2.wireOp",EDGE,"E0");Q88=makeQuery(id+"F3.opExtrude","CAP_EDGE",EDGE,{"disambiguationData":[OSD([subQ0]),TDD([makeQuery(id+"F2.imprint","IMPRINT",EDGE,{"disambiguationData":[TD([[makeQuery(id+"F2.imprint","INTERSECT",VERTEX,{"derivedFrom":[subQ0,sQuery(id+"F2.wireOp",EDGE,"E13.17.2")]}),-1.0]])],"derivedFrom":subQ0})])],"isStart":true});}
            var Q89;
            Q89=makeQuery(id+"F3.opExtrude","CAP_EDGE",EDGE,{"disambiguationData":[OSD([sQuery(id+"F2.wireOp",EDGE,"E13.17.2")])],"isStart":true});
            var Q90;
            Q90=makeQuery(id+"F3.opExtrude","CAP_EDGE",EDGE,{"disambiguationData":[OSD([sQuery(id+"F2.wireOp",EDGE,"E13.17.0")])],"isStart":true});
            var Q91;
            {var subQ0=sQuery(id+"F2.wireOp",EDGE,"E0");Q91=makeQuery(id+"F3.opExtrude","CAP_EDGE",EDGE,{"disambiguationData":[OSD([subQ0]),TDD([makeQuery(id+"F2.imprint","IMPRINT",EDGE,{"disambiguationData":[TD([[makeQuery(id+"F2.imprint","INTERSECT",VERTEX,{"derivedFrom":[subQ0,sQuery(id+"F2.wireOp",EDGE,"E13.16.2")]}),-1.0]])],"derivedFrom":subQ0})])],"isStart":true});}
            var Q92;
            Q92=makeQuery(id+"F3.opExtrude","CAP_EDGE",EDGE,{"disambiguationData":[OSD([sQuery(id+"F2.wireOp",EDGE,"E13.16.2")])],"isStart":true});
            var Q93;
            Q93=makeQuery(id+"F3.opExtrude","CAP_EDGE",EDGE,{"disambiguationData":[OSD([sQuery(id+"F2.wireOp",EDGE,"E13.16.0")])],"isStart":true});
            var Q94;
            {var subQ0=sQuery(id+"F2.wireOp",EDGE,"E0");Q94=makeQuery(id+"F3.opExtrude","CAP_EDGE",EDGE,{"disambiguationData":[OSD([subQ0]),TDD([makeQuery(id+"F2.imprint","IMPRINT",EDGE,{"disambiguationData":[TD([[makeQuery(id+"F2.imprint","INTERSECT",VERTEX,{"derivedFrom":[subQ0,sQuery(id+"F2.wireOp",EDGE,"E13.15.2")]}),-1.0]])],"derivedFrom":subQ0})])],"isStart":true});}
            var Q95;
            Q95=makeQuery(id+"F3.opExtrude","CAP_EDGE",EDGE,{"disambiguationData":[OSD([sQuery(id+"F2.wireOp",EDGE,"E13.15.2")])],"isStart":true});
            var Q96;
            Q96=makeQuery(id+"F3.opExtrude","CAP_EDGE",EDGE,{"disambiguationData":[OSD([sQuery(id+"F2.wireOp",EDGE,"E13.15.0")])],"isStart":true});
            var Q97;
            {var subQ0=sQuery(id+"F2.wireOp",EDGE,"E0");Q97=makeQuery(id+"F3.opExtrude","CAP_EDGE",EDGE,{"disambiguationData":[OSD([subQ0]),TDD([makeQuery(id+"F2.imprint","IMPRINT",EDGE,{"disambiguationData":[TD([[makeQuery(id+"F2.imprint","INTERSECT",VERTEX,{"derivedFrom":[subQ0,sQuery(id+"F2.wireOp",EDGE,"E13.14.2")]}),-1.0]])],"derivedFrom":subQ0})])],"isStart":true});}
            var Q98;
            Q98=makeQuery(id+"F3.opExtrude","CAP_EDGE",EDGE,{"disambiguationData":[OSD([sQuery(id+"F2.wireOp",EDGE,"E13.14.2")])],"isStart":true});
            var Q99;
            Q99=makeQuery(id+"F3.opExtrude","CAP_EDGE",EDGE,{"disambiguationData":[OSD([sQuery(id+"F2.wireOp",EDGE,"E13.14.0")])],"isStart":true});
            var Q100;
            {var subQ0=sQuery(id+"F2.wireOp",EDGE,"E0");Q100=makeQuery(id+"F3.opExtrude","CAP_EDGE",EDGE,{"disambiguationData":[OSD([subQ0]),TDD([makeQuery(id+"F2.imprint","IMPRINT",EDGE,{"disambiguationData":[TD([[makeQuery(id+"F2.imprint","INTERSECT",VERTEX,{"derivedFrom":[subQ0,sQuery(id+"F2.wireOp",EDGE,"E13.13.2")]}),-1.0]])],"derivedFrom":subQ0})])],"isStart":true});}
            var Q101;
            Q101=makeQuery(id+"F3.opExtrude","CAP_EDGE",EDGE,{"disambiguationData":[OSD([sQuery(id+"F2.wireOp",EDGE,"E13.13.2")])],"isStart":true});
            var Q102;
            Q102=makeQuery(id+"F3.opExtrude","CAP_EDGE",EDGE,{"disambiguationData":[OSD([sQuery(id+"F2.wireOp",EDGE,"E13.13.0")])],"isStart":true});
            var Q103;
            {var subQ0=sQuery(id+"F2.wireOp",EDGE,"E0");Q103=makeQuery(id+"F3.opExtrude","CAP_EDGE",EDGE,{"disambiguationData":[OSD([subQ0]),TDD([makeQuery(id+"F2.imprint","IMPRINT",EDGE,{"disambiguationData":[TD([[makeQuery(id+"F2.imprint","INTERSECT",VERTEX,{"derivedFrom":[subQ0,sQuery(id+"F2.wireOp",EDGE,"E13.12.2")]}),-1.0]])],"derivedFrom":subQ0})])],"isStart":true});}
            var Q104;
            Q104=makeQuery(id+"F3.opExtrude","CAP_EDGE",EDGE,{"disambiguationData":[OSD([sQuery(id+"F2.wireOp",EDGE,"E13.12.2")])],"isStart":true});
            var Q105;
            Q105=makeQuery(id+"F3.opExtrude","CAP_EDGE",EDGE,{"disambiguationData":[OSD([sQuery(id+"F2.wireOp",EDGE,"E13.12.0")])],"isStart":true});
            var Q106;
            {var subQ0=sQuery(id+"F2.wireOp",EDGE,"E0");Q106=makeQuery(id+"F3.opExtrude","CAP_EDGE",EDGE,{"disambiguationData":[OSD([subQ0]),TDD([makeQuery(id+"F2.imprint","IMPRINT",EDGE,{"disambiguationData":[TD([[makeQuery(id+"F2.imprint","INTERSECT",VERTEX,{"derivedFrom":[subQ0,sQuery(id+"F2.wireOp",EDGE,"E13.11.2")]}),-1.0]])],"derivedFrom":subQ0})])],"isStart":true});}
            var Q107;
            Q107=makeQuery(id+"F3.opExtrude","CAP_EDGE",EDGE,{"disambiguationData":[OSD([sQuery(id+"F2.wireOp",EDGE,"E13.11.2")])],"isStart":true});
            var Q108;
            Q108=makeQuery(id+"F3.opExtrude","CAP_EDGE",EDGE,{"disambiguationData":[OSD([sQuery(id+"F2.wireOp",EDGE,"E13.11.0")])],"isStart":true});
            var Q109;
            {var subQ0=sQuery(id+"F2.wireOp",EDGE,"E0");Q109=makeQuery(id+"F3.opExtrude","CAP_EDGE",EDGE,{"disambiguationData":[OSD([subQ0]),TDD([makeQuery(id+"F2.imprint","IMPRINT",EDGE,{"disambiguationData":[TD([[makeQuery(id+"F2.imprint","INTERSECT",VERTEX,{"derivedFrom":[subQ0,sQuery(id+"F2.wireOp",EDGE,"E13.10.2")]}),-1.0]])],"derivedFrom":subQ0})])],"isStart":true});}
            var Q110;
            Q110=makeQuery(id+"F3.opExtrude","CAP_EDGE",EDGE,{"disambiguationData":[OSD([sQuery(id+"F2.wireOp",EDGE,"E13.10.2")])],"isStart":true});
            var Q111;
            Q111=makeQuery(id+"F3.opExtrude","CAP_EDGE",EDGE,{"disambiguationData":[OSD([sQuery(id+"F2.wireOp",EDGE,"E13.10.0")])],"isStart":true});
            var Q112;
            {var subQ0=sQuery(id+"F2.wireOp",EDGE,"E0");Q112=makeQuery(id+"F3.opExtrude","CAP_EDGE",EDGE,{"disambiguationData":[OSD([subQ0]),TDD([makeQuery(id+"F2.imprint","IMPRINT",EDGE,{"disambiguationData":[TD([[makeQuery(id+"F2.imprint","INTERSECT",VERTEX,{"derivedFrom":[subQ0,sQuery(id+"F2.wireOp",EDGE,"E13.9.2")]}),-1.0]])],"derivedFrom":subQ0})])],"isStart":true});}
            var Q113;
            Q113=makeQuery(id+"F3.opExtrude","CAP_EDGE",EDGE,{"disambiguationData":[OSD([sQuery(id+"F2.wireOp",EDGE,"E13.9.2")])],"isStart":true});
            var Q114;
            Q114=makeQuery(id+"F3.opExtrude","CAP_EDGE",EDGE,{"disambiguationData":[OSD([sQuery(id+"F2.wireOp",EDGE,"E13.9.0")])],"isStart":true});
            var Q115;
            {var subQ0=sQuery(id+"F2.wireOp",EDGE,"E0");Q115=makeQuery(id+"F3.opExtrude","CAP_EDGE",EDGE,{"disambiguationData":[OSD([subQ0]),TDD([makeQuery(id+"F2.imprint","IMPRINT",EDGE,{"disambiguationData":[TD([[makeQuery(id+"F2.imprint","INTERSECT",VERTEX,{"derivedFrom":[subQ0,sQuery(id+"F2.wireOp",EDGE,"E13.8.2")]}),-1.0]])],"derivedFrom":subQ0})])],"isStart":true});}
            var Q116;
            Q116=makeQuery(id+"F3.opExtrude","CAP_EDGE",EDGE,{"disambiguationData":[OSD([sQuery(id+"F2.wireOp",EDGE,"E13.8.2")])],"isStart":true});
            fillet(context, id + "F4", {"entities" : qUnion([Q0, Q1, Q2, Q3, Q4, Q5, Q6, Q7, Q8, Q9, Q10, Q11, Q12, Q13, Q14, Q15, Q16, Q17, Q18, Q19, Q20, Q21, Q22, Q23, Q24, Q25, Q26, Q27, Q28, Q29, Q30, Q31, Q32, Q33, Q34, Q35, Q36, Q37, Q38, Q39, Q40, Q41, Q42, Q43, Q44, Q45, Q46, Q47, Q48, Q49, Q50, Q51, Q52, Q53, Q54, Q55, Q56, Q57, Q58, Q59, Q60, Q61, Q62, Q63, Q64, Q65, Q66, Q67, Q68, Q69, Q70, Q71, Q72, Q73, Q74, Q75, Q76, Q77, Q78, Q79, Q80, Q81, Q82, Q83, Q84, Q85, Q86, Q87, Q88, Q89, Q90, Q91, Q92, Q93, Q94, Q95, Q96, Q97, Q98, Q99, Q100, Q101, Q102, Q103, Q104, Q105, Q106, Q107, Q108, Q109, Q110, Q111, Q112, Q113, Q114, Q115, Q116]), "radius" : (getVariable(context, 'TeethFillet')) * mm, "tangentPropagation" : true, "allowEdgeOverflow" : false});
        }
        {
            var Q0;
            Q0=makeQuery(id+"F3.opExtrude","CAP_FACE",FACE,{"disambiguationData":[OSD([sQuery(id+"F2.wireOp",EDGE,"E0"),sQuery(id+"F2.wireOp",EDGE,"E10.trimOffspring"),sQuery(id+"F2.wireOp",EDGE,"E11.MirrorCS"),sQuery(id+"F2.wireOp",EDGE,"E12"),sQuery(id+"F2.wireOp",EDGE,"E13.1.0"),sQuery(id+"F2.wireOp",EDGE,"E13.1.1"),sQuery(id+"F2.wireOp",EDGE,"E13.1.2"),sQuery(id+"F2.wireOp",EDGE,"E13.2.0"),sQuery(id+"F2.wireOp",EDGE,"E13.2.1"),sQuery(id+"F2.wireOp",EDGE,"E13.2.2"),sQuery(id+"F2.wireOp",EDGE,"E13.3.0"),sQuery(id+"F2.wireOp",EDGE,"E13.3.1"),sQuery(id+"F2.wireOp",EDGE,"E13.3.2"),sQuery(id+"F2.wireOp",EDGE,"E13.4.0"),sQuery(id+"F2.wireOp",EDGE,"E13.4.1"),sQuery(id+"F2.wireOp",EDGE,"E13.4.2"),sQuery(id+"F2.wireOp",EDGE,"E13.5.0"),sQuery(id+"F2.wireOp",EDGE,"E13.5.1"),sQuery(id+"F2.wireOp",EDGE,"E13.5.2"),sQuery(id+"F2.wireOp",EDGE,"E13.6.0"),sQuery(id+"F2.wireOp",EDGE,"E13.6.1"),sQuery(id+"F2.wireOp",EDGE,"E13.6.2"),sQuery(id+"F2.wireOp",EDGE,"E13.7.0"),sQuery(id+"F2.wireOp",EDGE,"E13.7.1"),sQuery(id+"F2.wireOp",EDGE,"E13.7.2"),sQuery(id+"F2.wireOp",EDGE,"E13.8.0"),sQuery(id+"F2.wireOp",EDGE,"E13.8.1"),sQuery(id+"F2.wireOp",EDGE,"E13.8.2"),sQuery(id+"F2.wireOp",EDGE,"E13.9.0"),sQuery(id+"F2.wireOp",EDGE,"E13.9.1"),sQuery(id+"F2.wireOp",EDGE,"E13.9.2"),sQuery(id+"F2.wireOp",EDGE,"E13.10.0"),sQuery(id+"F2.wireOp",EDGE,"E13.10.1"),sQuery(id+"F2.wireOp",EDGE,"E13.10.2"),sQuery(id+"F2.wireOp",EDGE,"E13.11.0"),sQuery(id+"F2.wireOp",EDGE,"E13.11.1"),sQuery(id+"F2.wireOp",EDGE,"E13.11.2"),sQuery(id+"F2.wireOp",EDGE,"E13.12.0"),sQuery(id+"F2.wireOp",EDGE,"E13.12.1"),sQuery(id+"F2.wireOp",EDGE,"E13.12.2"),sQuery(id+"F2.wireOp",EDGE,"E13.13.0"),sQuery(id+"F2.wireOp",EDGE,"E13.13.1"),sQuery(id+"F2.wireOp",EDGE,"E13.13.2"),sQuery(id+"F2.wireOp",EDGE,"E13.14.0"),sQuery(id+"F2.wireOp",EDGE,"E13.14.1"),sQuery(id+"F2.wireOp",EDGE,"E13.14.2"),sQuery(id+"F2.wireOp",EDGE,"E13.15.0"),sQuery(id+"F2.wireOp",EDGE,"E13.15.1"),sQuery(id+"F2.wireOp",EDGE,"E13.15.2"),sQuery(id+"F2.wireOp",EDGE,"E13.16.0"),sQuery(id+"F2.wireOp",EDGE,"E13.16.1"),sQuery(id+"F2.wireOp",EDGE,"E13.16.2"),sQuery(id+"F2.wireOp",EDGE,"E13.17.0"),sQuery(id+"F2.wireOp",EDGE,"E13.17.1"),sQuery(id+"F2.wireOp",EDGE,"E13.17.2"),sQuery(id+"F2.wireOp",EDGE,"E13.18.0"),sQuery(id+"F2.wireOp",EDGE,"E13.18.1"),sQuery(id+"F2.wireOp",EDGE,"E13.18.2"),sQuery(id+"F2.wireOp",EDGE,"E13.19.0"),sQuery(id+"F2.wireOp",EDGE,"E13.19.1"),sQuery(id+"F2.wireOp",EDGE,"E13.19.2"),sQuery(id+"F2.wireOp",EDGE,"E14")])],"isStart":false});
            var sketch = newSketch(context, id + "F5", { "sketchPlane" : qUnion([Q0])});
            skCircle(sketch, "E15", {"center": v(0, 0) * mm, "radius": 15.11 * mm});
            skSolve(sketch);
        }
        {
            var Q0;
            Q0=makeQuery(id+"F5.imprint","IMPRINT",FACE,{"disambiguationData":[TD([[makeQuery(id+"F5.imprint","IMPRINT",EDGE,{"derivedFrom":sQuery(id+"F5.wireOp",EDGE,"E15")}),1.0]])]});
            extrude(context, id + "F6", {"entities" : qUnion([Q0]), "depth" : 2.5 * mm, "offsetDistance" : 25 * mm});
        }
        {
            var Q0;
            Q0=makeQuery(id+"F6.opExtrude","SWEPT_BODY",BODY,{"disambiguationData":[OSD([sQuery(id+"F2.wireOp",EDGE,"E0"),sQuery(id+"F2.wireOp",EDGE,"E10.trimOffspring"),sQuery(id+"F2.wireOp",EDGE,"E11.MirrorCS"),sQuery(id+"F2.wireOp",EDGE,"E12"),sQuery(id+"F2.wireOp",EDGE,"E13.1.0"),sQuery(id+"F2.wireOp",EDGE,"E13.1.1"),sQuery(id+"F2.wireOp",EDGE,"E13.1.2"),sQuery(id+"F2.wireOp",EDGE,"E13.2.0"),sQuery(id+"F2.wireOp",EDGE,"E13.2.1"),sQuery(id+"F2.wireOp",EDGE,"E13.2.2"),sQuery(id+"F2.wireOp",EDGE,"E13.3.0"),sQuery(id+"F2.wireOp",EDGE,"E13.3.1"),sQuery(id+"F2.wireOp",EDGE,"E13.3.2"),sQuery(id+"F2.wireOp",EDGE,"E13.4.0"),sQuery(id+"F2.wireOp",EDGE,"E13.4.1"),sQuery(id+"F2.wireOp",EDGE,"E13.4.2"),sQuery(id+"F2.wireOp",EDGE,"E13.5.0"),sQuery(id+"F2.wireOp",EDGE,"E13.5.1"),sQuery(id+"F2.wireOp",EDGE,"E13.5.2"),sQuery(id+"F2.wireOp",EDGE,"E13.6.0"),sQuery(id+"F2.wireOp",EDGE,"E13.6.1"),sQuery(id+"F2.wireOp",EDGE,"E13.6.2"),sQuery(id+"F2.wireOp",EDGE,"E13.7.0"),sQuery(id+"F2.wireOp",EDGE,"E13.7.1"),sQuery(id+"F2.wireOp",EDGE,"E13.7.2"),sQuery(id+"F2.wireOp",EDGE,"E13.8.0"),sQuery(id+"F2.wireOp",EDGE,"E13.8.1"),sQuery(id+"F2.wireOp",EDGE,"E13.8.2"),sQuery(id+"F2.wireOp",EDGE,"E13.9.0"),sQuery(id+"F2.wireOp",EDGE,"E13.9.1"),sQuery(id+"F2.wireOp",EDGE,"E13.9.2"),sQuery(id+"F2.wireOp",EDGE,"E13.10.0"),sQuery(id+"F2.wireOp",EDGE,"E13.10.1"),sQuery(id+"F2.wireOp",EDGE,"E13.10.2"),sQuery(id+"F2.wireOp",EDGE,"E13.11.0"),sQuery(id+"F2.wireOp",EDGE,"E13.11.1"),sQuery(id+"F2.wireOp",EDGE,"E13.11.2"),sQuery(id+"F2.wireOp",EDGE,"E13.12.0"),sQuery(id+"F2.wireOp",EDGE,"E13.12.1"),sQuery(id+"F2.wireOp",EDGE,"E13.12.2"),sQuery(id+"F2.wireOp",EDGE,"E13.13.0"),sQuery(id+"F2.wireOp",EDGE,"E13.13.1"),sQuery(id+"F2.wireOp",EDGE,"E13.13.2"),sQuery(id+"F2.wireOp",EDGE,"E13.14.0"),sQuery(id+"F2.wireOp",EDGE,"E13.14.1"),sQuery(id+"F2.wireOp",EDGE,"E13.14.2"),sQuery(id+"F2.wireOp",EDGE,"E13.15.0"),sQuery(id+"F2.wireOp",EDGE,"E13.15.1"),sQuery(id+"F2.wireOp",EDGE,"E13.15.2"),sQuery(id+"F2.wireOp",EDGE,"E13.16.0"),sQuery(id+"F2.wireOp",EDGE,"E13.16.1"),sQuery(id+"F2.wireOp",EDGE,"E13.16.2"),sQuery(id+"F2.wireOp",EDGE,"E13.17.0"),sQuery(id+"F2.wireOp",EDGE,"E13.17.1"),sQuery(id+"F2.wireOp",EDGE,"E13.17.2"),sQuery(id+"F2.wireOp",EDGE,"E13.18.0"),sQuery(id+"F2.wireOp",EDGE,"E13.18.1"),sQuery(id+"F2.wireOp",EDGE,"E13.18.2"),sQuery(id+"F2.wireOp",EDGE,"E13.19.0"),sQuery(id+"F2.wireOp",EDGE,"E13.19.1"),sQuery(id+"F2.wireOp",EDGE,"E13.19.2"),sQuery(id+"F2.wireOp",EDGE,"E14"),sQuery(id+"F5.wireOp",EDGE,"E15")])]});
            deleteBodies(context, id + "F7", {"entities" : qUnion([Q0])});
        }
    });
